# Revit family: Cable plug_IP67_RFA_2
name_source: partatom
category: Pipe Accessories
units: mm (PartAtom-declared; Revit-internal decimal feet)

## family parameters
Always vertical = Yes
Cut with Voids When Loaded = No
OmniClass Number = 23.65.55.14.17
OmniClass Title = Adjusting/Controlling Valves for Liquid Services
Part Type = Normal
Round Connector Dimension = Use Diameter
Shared = Yes
Work Plane-Based = No

## types (1)
- Cable plug IP67_042N1256
    Body Material = Danfoss Polyamide Gray (GF reinforced)
    Description = Cable plug
    H = 28 mm  [stored 0.0918635 ft]
    IfcExportAs = IfcValveType
    IfcExportType = Cable plug
    L = 32 mm
    Manufacturer = Danfoss
    Model = 042N1256
    Model Type = Cable plug IP67
    URL = https://store.danfoss.com
    W = 50 mm  [stored 0.164042 ft]
    Weight = 0.03 kg

note: [stored X ft] marks values corroborated as IEEE doubles in the binary element streams (Revit-internal decimal feet)

## geometry (parser evidence)
native form markers: Sweep x2
no freeform markers — native parametric forms only
